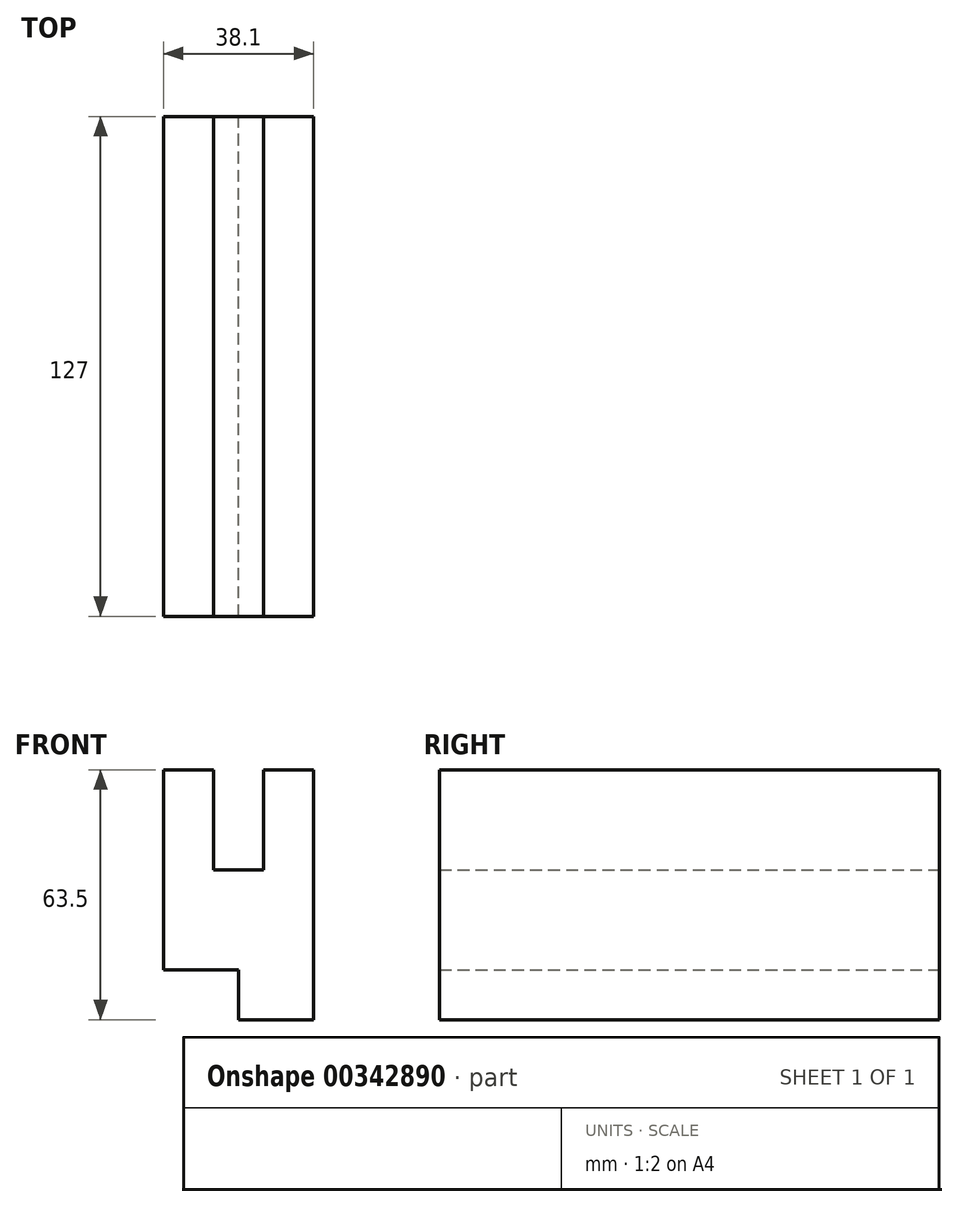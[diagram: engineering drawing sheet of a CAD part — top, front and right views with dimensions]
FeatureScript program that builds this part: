
annotation { "Feature Type Name" : "Feature", "Feature Type Description" : "" }
export const myFeature = defineFeature(function(context is Context, id is Id, definition is map)
    precondition{}
    {
        {
            var Q0;
            Q0=qCreatedBy(makeId("Front.planeOp"),FACE);
            var sketch = newSketch(context, id + "F0", { "sketchPlane" : qUnion([Q0])});
            skLineSegment(sketch, "E0", {"start": v(-68.2, 37.2) * mm, "end": v(-68.2, -13.6) * mm});
            skLineSegment(sketch, "E1", {"start": v(-68.2, -13.6) * mm, "end": v(-49.16, -13.6) * mm});
            skLineSegment(sketch, "E2", {"start": v(-49.16, -13.6) * mm, "end": v(-49.16, -26.3) * mm});
            skLineSegment(sketch, "E3", {"start": v(-49.16, -26.3) * mm, "end": v(-30.1, -26.3) * mm});
            skLineSegment(sketch, "E4", {"start": v(-30.1, -26.3) * mm, "end": v(-30.1, 37.2) * mm});
            skLineSegment(sketch, "E5", {"start": v(-30.1, 37.2) * mm, "end": v(-42.8, 37.2) * mm});
            skLineSegment(sketch, "E6", {"start": v(-68.2, 37.2) * mm, "end": v(-55.5, 37.2) * mm});
            skLineSegment(sketch, "E7", {"start": v(-55.5, 37.2) * mm, "end": v(-55.5, 11.8) * mm});
            skLineSegment(sketch, "E8", {"start": v(-55.5, 11.8) * mm, "end": v(-42.8, 11.8) * mm});
            skLineSegment(sketch, "E9", {"start": v(-42.8, 11.8) * mm, "end": v(-42.8, 37.2) * mm});
            skSolve(sketch);
        }
        {
            var Q0;
            Q0=makeQuery(id+"F0.imprint","IMPRINT",FACE,{"disambiguationData":[TD([[makeQuery(id+"F0.imprint","IMPRINT",EDGE,{"derivedFrom":sQuery(id+"F0.wireOp",EDGE,"E0")}),1.0]])]});
            extrude(context, id + "F1", {"entities" : qUnion([Q0]), "depth" : 127 * mm});
        }
    });
